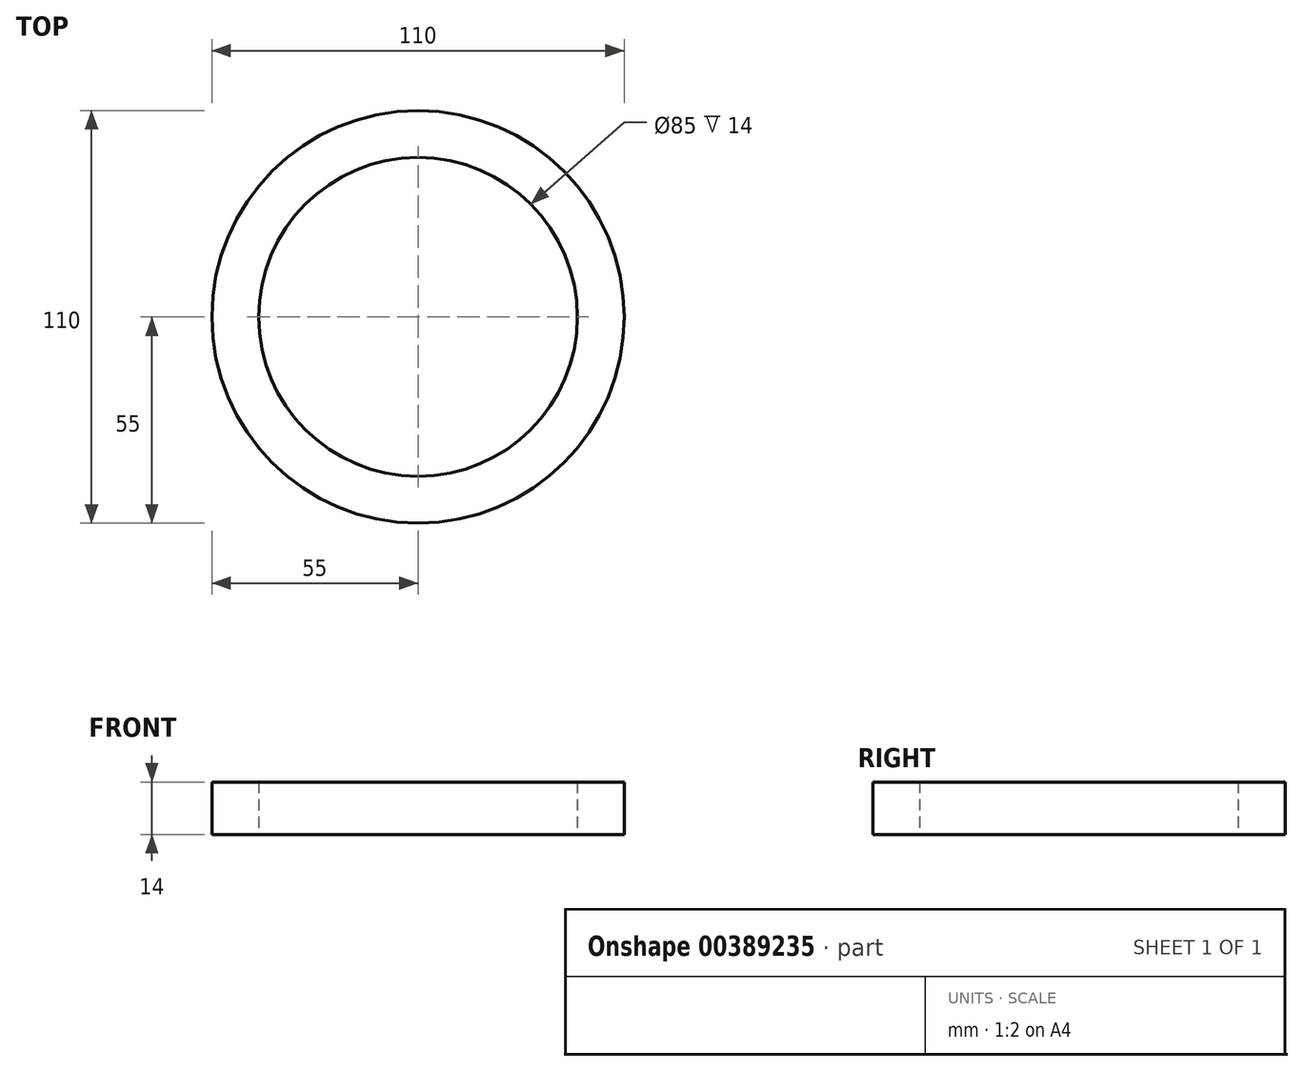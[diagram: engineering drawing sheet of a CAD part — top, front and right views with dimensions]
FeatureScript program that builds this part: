
annotation { "Feature Type Name" : "Feature", "Feature Type Description" : "" }
export const myFeature = defineFeature(function(context is Context, id is Id, definition is map)
    precondition{}
    {
        {
            var Q0;
            Q0=qCreatedBy(makeId("Top.planeOp"),FACE);
            var sketch = newSketch(context, id + "F0", { "sketchPlane" : qUnion([Q0])});
            skCircle(sketch, "E0", {"center": v(0, 0) * mm, "radius": 42.5 * mm});
            skCircle(sketch, "E1.0", {"center": v(0, 0) * mm, "radius": 55 * mm});
            skSolve(sketch);
        }
        {
            var Q0;
            Q0=makeQuery(id+"F0.imprint","IMPRINT",FACE,{"disambiguationData":[TD([[makeQuery(id+"F0.imprint","IMPRINT",EDGE,{"derivedFrom":sQuery(id+"F0.wireOp",EDGE,"E0")}),-1.0]])]});
            extrude(context, id + "F1", {"entities" : qUnion([Q0]), "depth" : 14 * mm});
        }
    });
